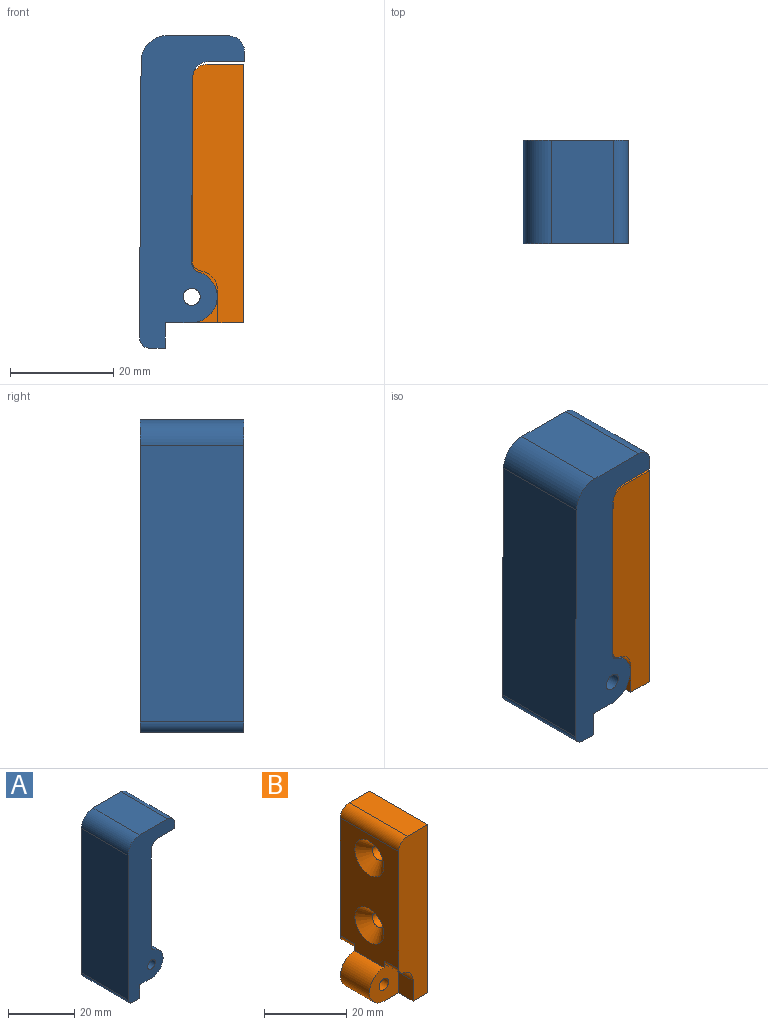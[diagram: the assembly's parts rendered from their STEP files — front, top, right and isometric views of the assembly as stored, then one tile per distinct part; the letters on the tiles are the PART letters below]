
ASSEMBLY  parts=2 mates=1
PART A: 24 faces, bbox 20x20x60.5 mm
  f0: plane 37.5x20mm, normal (1,0,0), area 732.9mm2, adj f5,f6,f8,f9,f10,f18,f19,f23
  f1: plane 53.5x20mm, normal (-1,0,0), area 1070mm2, adj f5,f6,f21,f22
  f2: plane 5x5mm, normal (0,0,-1), area 25mm2, adj f6,f8,f11,f12
  f3: plane 5x5mm, normal (0,0,-1), area 25mm2, adj f5,f9,f11,f13
  f4: cylinder r=1.65mm len=5mm, axis (0,-1,0), area 51.8mm2, adj f5,f9
  f5: plane 60.5x20mm, normal (0,1,0), area 655mm2, adj f0,f1,f3,f4,f11,f13,f14,f15
  f6: plane 60.5x20mm, normal (0,-1,0), area 655mm2, adj f0,f1,f2,f7,f11,f12,f14,f15
  f7: cylinder r=1.65mm len=5mm, axis (0,-1,0), area 51.8mm2, adj f6,f8
  f8: plane 11.71x10mm, normal (0,1,0), area 81.2mm2, adj f0,f2,f7,f10,f11,f12,f18
  f9: plane 11.71x10mm, normal (0,-1,0), area 81.2mm2, adj f0,f3,f4,f10,f11,f13,f19
  f10: plane 10x5mm, normal (0,0,-1), area 50mm2, adj f0,f8,f9,f11
  f11: plane 20x15mm, normal (1,0,0), area 200mm2, adj f2,f3,f5,f6,f8,f9,f10,f14
  f12: cylinder r=5mm len=9.79mm, axis (0,-1,0), area 71.3mm2, adj f2,f6,f8,f18
  f13: cylinder r=5mm len=9.79mm, axis (0,-1,0), area 71.3mm2, adj f3,f5,f9,f19
  f14: plane 20x3mm, normal (0,0,-1), area 60mm2, adj f5,f6,f11,f22
  f15: plane 20x12mm, normal (0,0,1), area 240mm2, adj f5,f6,f20,f21
  f16: plane 20x7mm, normal (0,0,-1), area 140mm2, adj f5,f6,f17,f23
  f17: plane 20x2mm, normal (1,0,0), area 40mm2, adj f5,f6,f16,f20
  f18: cylinder r=2mm len=5mm, axis (0,-1,0), area 12.8mm2, adj f0,f6,f8,f12
  f19: cylinder r=2mm len=5mm, axis (0,-1,0), area 12.8mm2, adj f0,f5,f9,f13
  f20: cylinder r=3mm len=20mm, axis (0,1,0), area 94.2mm2, adj f5,f6,f15,f17
  f21: cylinder r=5mm len=20mm, axis (0,-1,0), area 157.1mm2, adj f1,f5,f6,f15
  f22: cylinder r=2mm len=20mm, axis (0,1,0), area 62.8mm2, adj f1,f5,f6,f14
  f23: cylinder r=3mm len=20mm, axis (0,1,0), area 94.2mm2, adj f0,f5,f6,f16
PART B: 21 faces, bbox 15x20x50 mm
  f0: plane 50x10mm, normal (0,-1,0), area 450.4mm2, adj f1,f2,f4,f5,f7,f12,f13,f15
  f1: plane 20x10mm, normal (0,0,-1), area 150mm2, adj f0,f2,f3,f6,f7,f8,f9,f11
  f2: plane 50x20mm, normal (1,0,0), area 974.9mm2, adj f0,f1,f3,f5,f17,f18
  f3: plane 50x10mm, normal (0,1,0), area 450.4mm2, adj f1,f2,f4,f5,f9,f12,f14,f16
  f4: plane 37x20mm, normal (-1,0,0), area 562.9mm2, adj f0,f3,f6,f8,f11,f12,f13,f14
  f5: plane 20x7mm, normal (0,0,1), area 140mm2, adj f0,f2,f3,f12
  f6: plane 12x10mm, normal (0,-1,0), area 78.4mm2, adj f1,f4,f7,f10,f11,f13,f15
  f7: plane 6.08x5mm, normal (-1,0,0), area 30.4mm2, adj f0,f1,f6,f15
  f8: plane 12x10mm, normal (0,1,0), area 78.4mm2, adj f1,f4,f9,f10,f11,f14,f16
  f9: plane 6.08x5mm, normal (-1,0,0), area 30.4mm2, adj f1,f3,f8,f16
  f10: cylinder r=1.65mm len=10mm, axis (0,-1,0), area 103.7mm2, adj f6,f8
  f11: cylinder r=5mm len=10mm, axis (0,-1,0), area 157.1mm2, adj f1,f4,f6,f8
  f12: cylinder r=3mm len=20mm, axis (0,1,0), area 94.2mm2, adj f0,f3,f4,f5
  f13: cylinder r=2mm len=5mm, axis (0,1,0), area 14mm2, adj f0,f4,f6,f15
  f14: cylinder r=2mm len=5mm, axis (0,1,0), area 14mm2, adj f3,f4,f8,f16
  f15: cylinder r=4mm len=5mm, axis (0,1,0), area 28.1mm2, adj f0,f6,f7,f13
  f16: cylinder r=4mm len=5mm, axis (0,1,0), area 28.1mm2, adj f3,f8,f9,f14
  f17: cylinder r=2mm len=7mm, axis (-1,0,0), area 88mm2, adj f2,f19
  f18: cylinder r=2mm len=7mm, axis (-1,0,0), area 88mm2, adj f2,f20
  f19: cone r=2mm half-angle=45deg, axis (-1,0,0), area 93.3mm2, adj f4,f17
  f20: cone r=2mm half-angle=45deg, axis (-1,0,0), area 93.3mm2, adj f4,f18
PLACE A rot(axis=(0,1,0),0.3deg) t=(-0.03,0,0.13)mm
PLACE B at identity fixed
MATE revolute A.f4 <-> B.f10  axis (0,1,0) through (22.44,-5,5)mm
